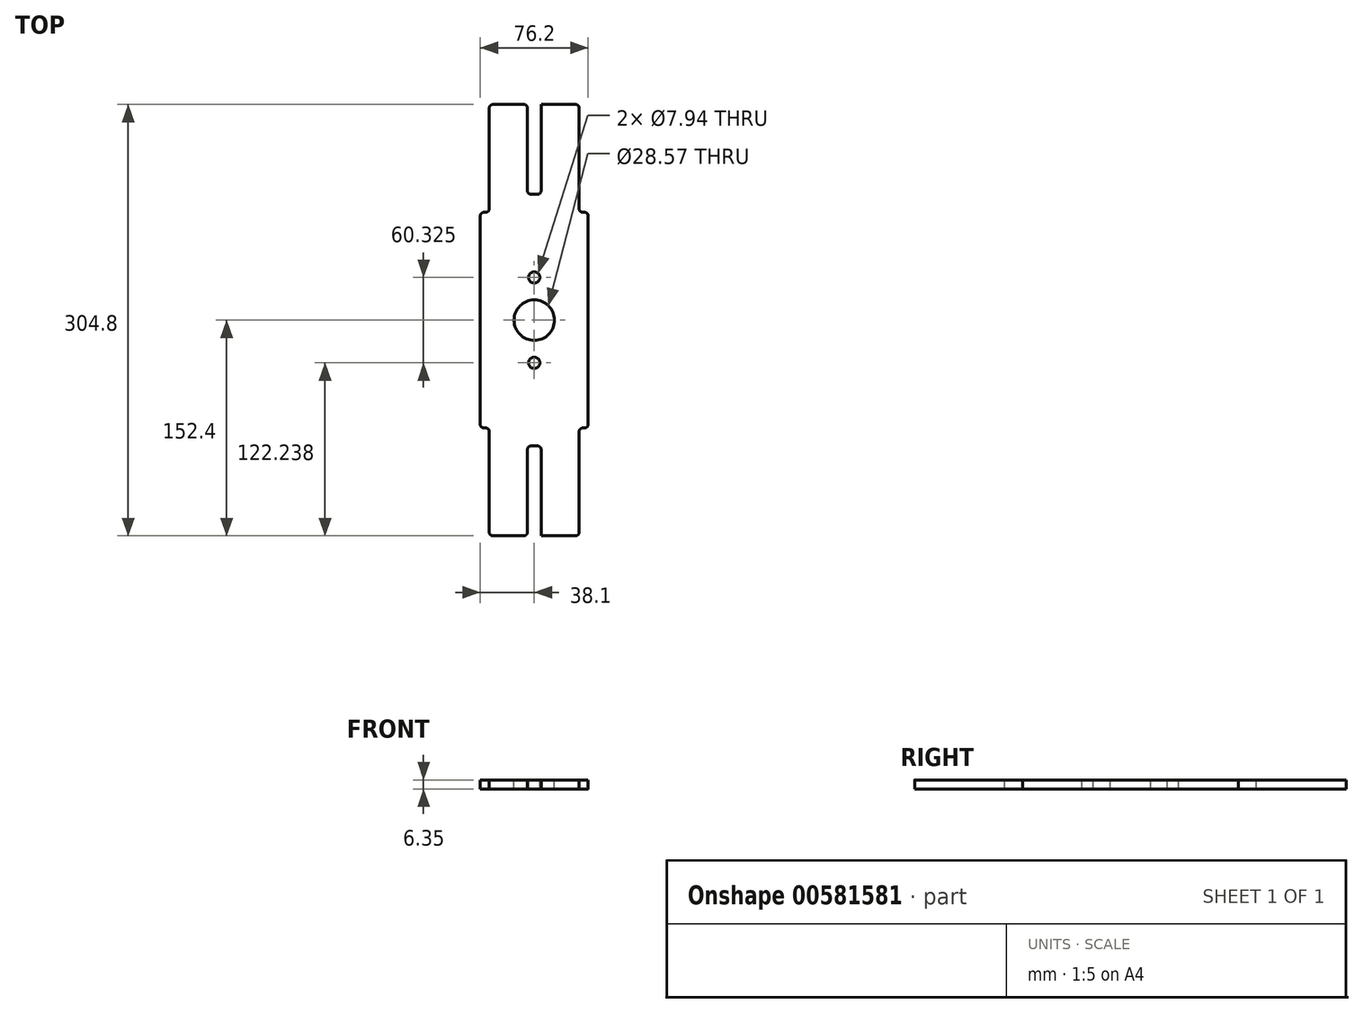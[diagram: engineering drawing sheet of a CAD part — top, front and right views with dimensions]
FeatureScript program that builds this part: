
annotation { "Feature Type Name" : "Feature", "Feature Type Description" : "" }
export const myFeature = defineFeature(function(context is Context, id is Id, definition is map)
    precondition{}
    {
        {
            var Q0;
            Q0=qCreatedBy(makeId("Top.planeOp"),FACE);
            var sketch = newSketch(context, id + "F0", { "sketchPlane" : qUnion([Q0])});
            skLineSegment(sketch, "E0.bottom", {"start": v(31.75, 152.4) * mm, "end": v(-31.75, 152.4) * mm});
            skLineSegment(sketch, "E0.top", {"start": v(31.75, -152.4) * mm, "end": v(-31.75, -152.4) * mm});
            skLineSegment(sketch, "E0.left", {"start": v(31.75, 152.4) * mm, "end": v(31.75, -152.4) * mm});
            skLineSegment(sketch, "E0.right", {"start": v(-31.75, 152.4) * mm, "end": v(-31.75, -152.4) * mm});
            skPoint(sketch, "E0.middle", {"position": v(0, 0) * mm});
            skSolve(sketch);
        }
        {
            var Q0;
            Q0=makeQuery(id+"F0.imprint","IMPRINT",FACE,{"disambiguationData":[TD([[makeQuery(id+"F0.imprint","IMPRINT",EDGE,{"derivedFrom":sQuery(id+"F0.wireOp",EDGE,"E0.bottom")}),1.0]])]});
            extrude(context, id + "F1", {"entities" : qUnion([Q0]), "depth" : 6.35 * mm, "offsetDistance" : 25.4 * mm});
        }
        {
            var Q0;
            Q0=qCreatedBy(makeId("Top.planeOp"),FACE);
            var sketch = newSketch(context, id + "F2", { "sketchPlane" : qUnion([Q0])});
            skLineSegment(sketch, "E1.bottom", {"start": v(38.1, 76.2) * mm, "end": v(-38.1, 76.2) * mm});
            skLineSegment(sketch, "E1.top", {"start": v(38.1, -76.2) * mm, "end": v(-38.1, -76.2) * mm});
            skLineSegment(sketch, "E1.left", {"start": v(38.1, 76.2) * mm, "end": v(38.1, -76.2) * mm});
            skLineSegment(sketch, "E1.right", {"start": v(-38.1, 76.2) * mm, "end": v(-38.1, -76.2) * mm});
            skPoint(sketch, "E1.middle", {"position": v(0, 0) * mm});
            skSolve(sketch);
        }
        {
            var Q0;
            Q0=makeQuery(id+"F2.imprint","IMPRINT",FACE,{"disambiguationData":[TD([[makeQuery(id+"F2.imprint","IMPRINT",EDGE,{"derivedFrom":sQuery(id+"F2.wireOp",EDGE,"E1.bottom")}),1.0]])]});
            extrude(context, id + "F3", {"entities" : qUnion([Q0]), "operationType" : NewBodyOperationType.ADD, "depth" : 6.35 * mm, "offsetDistance" : 25.4 * mm});
        }
        {
            var Q0;
            Q0=makeQuery(id+"F3.boolean.opBoolean","MERGE",FACE,{"derivedFrom":[makeQuery(id+"F1.opExtrude","CAP_FACE",FACE,{"disambiguationData":[OSD([sQuery(id+"F0.wireOp",EDGE,"E0.bottom"),sQuery(id+"F0.wireOp",EDGE,"E0.top"),sQuery(id+"F0.wireOp",EDGE,"E0.left"),sQuery(id+"F0.wireOp",EDGE,"E0.right")])],"isStart":false}),makeQuery(id+"F3.opExtrude","CAP_FACE",FACE,{"disambiguationData":[OSD([sQuery(id+"F2.wireOp",EDGE,"E1.bottom"),sQuery(id+"F2.wireOp",EDGE,"E1.top"),sQuery(id+"F2.wireOp",EDGE,"E1.left"),sQuery(id+"F2.wireOp",EDGE,"E1.right")])],"isStart":false})]});
            var sketch = newSketch(context, id + "F4", { "sketchPlane" : qUnion([Q0])});
            skLineSegment(sketch, "E2.bottom", {"start": v(-4.83, 152.4) * mm, "end": v(4.83, 152.4) * mm});
            skLineSegment(sketch, "E2.top", {"start": v(-4.83, 88.9) * mm, "end": v(4.83, 88.9) * mm});
            skLineSegment(sketch, "E2.left", {"start": v(-4.83, 152.4) * mm, "end": v(-4.83, 88.9) * mm});
            skLineSegment(sketch, "E2.right", {"start": v(4.83, 152.4) * mm, "end": v(4.83, 88.9) * mm});
            skLineSegment(sketch, "E3.bottom", {"start": v(-4.83, -152.4) * mm, "end": v(4.83, -152.4) * mm});
            skLineSegment(sketch, "E3.top", {"start": v(-4.83, -88.9) * mm, "end": v(4.83, -88.9) * mm});
            skLineSegment(sketch, "E3.left", {"start": v(-4.83, -152.4) * mm, "end": v(-4.83, -88.9) * mm});
            skLineSegment(sketch, "E3.right", {"start": v(4.83, -152.4) * mm, "end": v(4.83, -88.9) * mm});
            skCircle(sketch, "E4", {"center": v(0, 0) * mm, "radius": 14.29 * mm});
            skCircle(sketch, "E5", {"center": v(0, 30.16) * mm, "radius": 3.97 * mm});
            skCircle(sketch, "E6", {"center": v(0, -30.16) * mm, "radius": 3.97 * mm});
            skSolve(sketch);
        }
        {
            var Q0;
            Q0 = qSketchRegion(id + "F4", true);
            extrude(context, id + "F5", {"entities" : qUnion([Q0]), "operationType" : NewBodyOperationType.REMOVE, "endBound" : BoundingType.THROUGH_ALL, "oppositeDirection" : true, "depth" : 25.4 * mm, "offsetDistance" : 25.4 * mm});
        }
        {
            var Q0;
            Q0=makeQuery(id+"F3.opExtrude","SWEPT_EDGE",EDGE,{"disambiguationData":[OSD([sQuery(id+"F2.wireOp",EDGE,"E1.bottom"),sQuery(id+"F2.wireOp",EDGE,"E1.right")])]});
            var Q1;
            Q1=makeQuery(id+"F3.boolean.opBoolean","INTERSECT",EDGE,{"derivedFrom":[makeQuery(id+"F1.opExtrude","SWEPT_FACE",FACE,{"disambiguationData":[OSD([sQuery(id+"F0.wireOp",EDGE,"E0.right")])]}),makeQuery(id+"F3.opExtrude","SWEPT_FACE",FACE,{"disambiguationData":[OSD([sQuery(id+"F2.wireOp",EDGE,"E1.bottom")])]})]});
            var Q2;
            Q2=makeQuery(id+"F1.opExtrude","SWEPT_EDGE",EDGE,{"disambiguationData":[OSD([sQuery(id+"F0.wireOp",EDGE,"E0.bottom"),sQuery(id+"F0.wireOp",EDGE,"E0.right")])]});
            var Q3;
            Q3=makeQuery(id+"F5.boolean.opBoolean","COPY",EDGE,{"derivedFrom":makeQuery(id+"F5.opExtrude","SWEPT_EDGE",EDGE,{"disambiguationData":[OSD([sQuery(id+"F0.wireOp",EDGE,"E0.bottom"),sQuery(id+"F4.wireOp",EDGE,"E2.bottom"),sQuery(id+"F4.wireOp",EDGE,"E2.left")])]})});
            var Q4;
            Q4=makeQuery(id+"F5.boolean.opBoolean","COPY",EDGE,{"derivedFrom":makeQuery(id+"F5.opExtrude","SWEPT_EDGE",EDGE,{"disambiguationData":[OSD([sQuery(id+"F0.wireOp",EDGE,"E0.bottom"),sQuery(id+"F4.wireOp",EDGE,"E2.bottom"),sQuery(id+"F4.wireOp",EDGE,"E2.right")])]})});
            var Q5;
            Q5=makeQuery(id+"F5.boolean.opBoolean","COPY",EDGE,{"derivedFrom":makeQuery(id+"F5.opExtrude","SWEPT_EDGE",EDGE,{"disambiguationData":[OSD([sQuery(id+"F4.wireOp",EDGE,"E2.top"),sQuery(id+"F4.wireOp",EDGE,"E2.right")])]})});
            var Q6;
            Q6=makeQuery(id+"F5.boolean.opBoolean","COPY",EDGE,{"derivedFrom":makeQuery(id+"F5.opExtrude","SWEPT_EDGE",EDGE,{"disambiguationData":[OSD([sQuery(id+"F4.wireOp",EDGE,"E2.top"),sQuery(id+"F4.wireOp",EDGE,"E2.left")])]})});
            var Q7;
            Q7=makeQuery(id+"F1.opExtrude","SWEPT_EDGE",EDGE,{"disambiguationData":[OSD([sQuery(id+"F0.wireOp",EDGE,"E0.bottom"),sQuery(id+"F0.wireOp",EDGE,"E0.left")])]});
            var Q8;
            Q8=makeQuery(id+"F3.boolean.opBoolean","INTERSECT",EDGE,{"derivedFrom":[makeQuery(id+"F1.opExtrude","SWEPT_FACE",FACE,{"disambiguationData":[OSD([sQuery(id+"F0.wireOp",EDGE,"E0.left")])]}),makeQuery(id+"F3.opExtrude","SWEPT_FACE",FACE,{"disambiguationData":[OSD([sQuery(id+"F2.wireOp",EDGE,"E1.bottom")])]})]});
            var Q9;
            Q9=makeQuery(id+"F3.opExtrude","SWEPT_EDGE",EDGE,{"disambiguationData":[OSD([sQuery(id+"F2.wireOp",EDGE,"E1.bottom"),sQuery(id+"F2.wireOp",EDGE,"E1.left")])]});
            var Q10;
            Q10=makeQuery(id+"F3.opExtrude","SWEPT_EDGE",EDGE,{"disambiguationData":[OSD([sQuery(id+"F2.wireOp",EDGE,"E1.top"),sQuery(id+"F2.wireOp",EDGE,"E1.left")])]});
            var Q11;
            Q11=makeQuery(id+"F3.boolean.opBoolean","INTERSECT",EDGE,{"derivedFrom":[makeQuery(id+"F1.opExtrude","SWEPT_FACE",FACE,{"disambiguationData":[OSD([sQuery(id+"F0.wireOp",EDGE,"E0.left")])]}),makeQuery(id+"F3.opExtrude","SWEPT_FACE",FACE,{"disambiguationData":[OSD([sQuery(id+"F2.wireOp",EDGE,"E1.top")])]})]});
            var Q12;
            Q12=makeQuery(id+"F1.opExtrude","SWEPT_EDGE",EDGE,{"disambiguationData":[OSD([sQuery(id+"F0.wireOp",EDGE,"E0.top"),sQuery(id+"F0.wireOp",EDGE,"E0.left")])]});
            var Q13;
            Q13=makeQuery(id+"F5.boolean.opBoolean","COPY",EDGE,{"derivedFrom":makeQuery(id+"F5.opExtrude","SWEPT_EDGE",EDGE,{"disambiguationData":[OSD([sQuery(id+"F0.wireOp",EDGE,"E0.top"),sQuery(id+"F4.wireOp",EDGE,"E3.bottom"),sQuery(id+"F4.wireOp",EDGE,"E3.right")])]})});
            var Q14;
            Q14=makeQuery(id+"F5.boolean.opBoolean","COPY",EDGE,{"derivedFrom":makeQuery(id+"F5.opExtrude","SWEPT_EDGE",EDGE,{"disambiguationData":[OSD([sQuery(id+"F4.wireOp",EDGE,"E3.top"),sQuery(id+"F4.wireOp",EDGE,"E3.right")])]})});
            var Q15;
            Q15=makeQuery(id+"F5.boolean.opBoolean","COPY",EDGE,{"derivedFrom":makeQuery(id+"F5.opExtrude","SWEPT_EDGE",EDGE,{"disambiguationData":[OSD([sQuery(id+"F4.wireOp",EDGE,"E3.top"),sQuery(id+"F4.wireOp",EDGE,"E3.left")])]})});
            var Q16;
            Q16=makeQuery(id+"F5.boolean.opBoolean","COPY",EDGE,{"derivedFrom":makeQuery(id+"F5.opExtrude","SWEPT_EDGE",EDGE,{"disambiguationData":[OSD([sQuery(id+"F0.wireOp",EDGE,"E0.top"),sQuery(id+"F4.wireOp",EDGE,"E3.bottom"),sQuery(id+"F4.wireOp",EDGE,"E3.left")])]})});
            var Q17;
            Q17=makeQuery(id+"F1.opExtrude","SWEPT_EDGE",EDGE,{"disambiguationData":[OSD([sQuery(id+"F0.wireOp",EDGE,"E0.top"),sQuery(id+"F0.wireOp",EDGE,"E0.right")])]});
            var Q18;
            Q18=makeQuery(id+"F3.boolean.opBoolean","INTERSECT",EDGE,{"derivedFrom":[makeQuery(id+"F1.opExtrude","SWEPT_FACE",FACE,{"disambiguationData":[OSD([sQuery(id+"F0.wireOp",EDGE,"E0.right")])]}),makeQuery(id+"F3.opExtrude","SWEPT_FACE",FACE,{"disambiguationData":[OSD([sQuery(id+"F2.wireOp",EDGE,"E1.top")])]})]});
            var Q19;
            Q19=makeQuery(id+"F3.opExtrude","SWEPT_EDGE",EDGE,{"disambiguationData":[OSD([sQuery(id+"F2.wireOp",EDGE,"E1.top"),sQuery(id+"F2.wireOp",EDGE,"E1.right")])]});
            fillet(context, id + "F6", {"entities" : qUnion([Q0, Q1, Q2, Q3, Q4, Q5, Q6, Q7, Q8, Q9, Q10, Q11, Q12, Q13, Q14, Q15, Q16, Q17, Q18, Q19]), "radius" : 2.54 * mm, "tangentPropagation" : true, "allowEdgeOverflow" : false});
        }
    });
